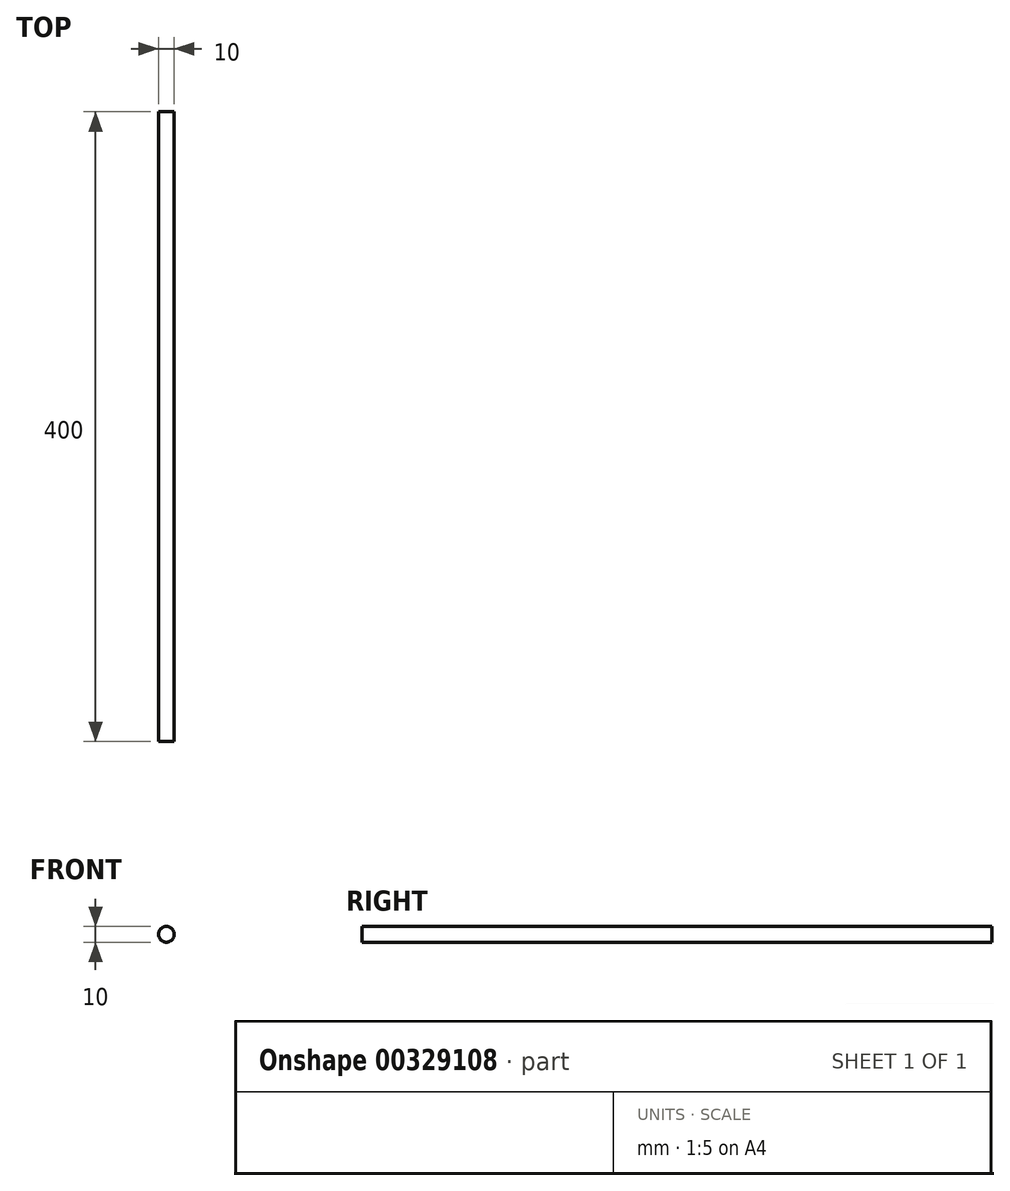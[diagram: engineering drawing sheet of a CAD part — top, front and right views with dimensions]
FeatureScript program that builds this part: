
annotation { "Feature Type Name" : "Feature", "Feature Type Description" : "" }
export const myFeature = defineFeature(function(context is Context, id is Id, definition is map)
    precondition{}
    {
        {
            var Q0;
            Q0=qCreatedBy(makeId("Front.planeOp"),FACE);
            var sketch = newSketch(context, id + "F0", { "sketchPlane" : qUnion([Q0])});
            skCircle(sketch, "E0", {"center": v(0, 0) * mm, "radius": 5 * mm});
            skSolve(sketch);
        }
        {
            var Q0;
            Q0 = qSketchRegion(id + "F0", true);
            extrude(context, id + "F1", {"entities" : qUnion([Q0]), "depth" : 400 * mm});
        }
    });
